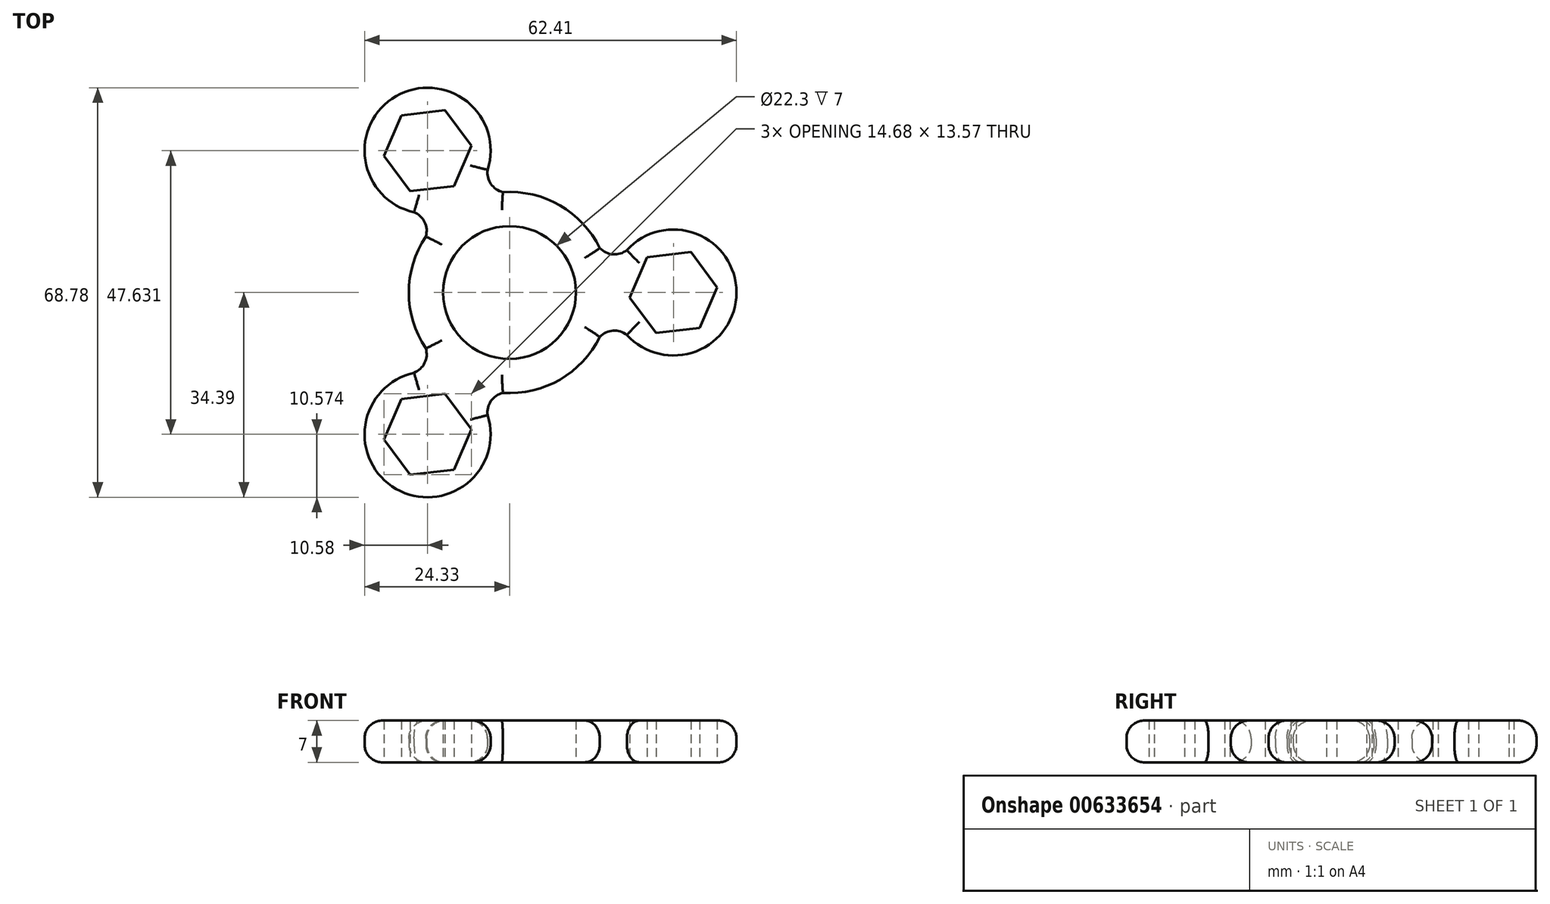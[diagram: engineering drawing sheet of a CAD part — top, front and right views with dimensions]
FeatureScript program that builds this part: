
annotation { "Feature Type Name" : "Feature", "Feature Type Description" : "" }
export const myFeature = defineFeature(function(context is Context, id is Id, definition is map)
    precondition{}
    {
        {
            var Q0;
            Q0=qCreatedBy(makeId("Top.planeOp"),FACE);
            var sketch = newSketch(context, id + "F0", { "sketchPlane" : qUnion([Q0])});
            skCircle(sketch, "E0", {"center": v(0, 0) * mm, "radius": 11.15 * mm});
            skCircle(sketch, "E1.cCircle", {"center": v(27.5, 0) * mm, "radius": 6.4 * mm, "construction": true});
            skLineSegment(sketch, "E1.0", {"start": v(34.84, 0.86) * mm, "end": v(31.91, -5.93) * mm});
            skLineSegment(sketch, "E1.1", {"start": v(31.91, -5.93) * mm, "end": v(24.57, -6.79) * mm});
            skLineSegment(sketch, "E1.2", {"start": v(24.57, -6.79) * mm, "end": v(20.16, -0.86) * mm});
            skLineSegment(sketch, "E1.3", {"start": v(20.16, -0.86) * mm, "end": v(23.09, 5.93) * mm});
            skLineSegment(sketch, "E1.4", {"start": v(23.09, 5.93) * mm, "end": v(30.43, 6.79) * mm});
            skLineSegment(sketch, "E1.5", {"start": v(30.43, 6.79) * mm, "end": v(34.84, 0.86) * mm});
            skPoint(sketch, "E1.0.midPoint", {"position": v(33.38, -2.54) * mm});
            skCircle(sketch, "E2", {"center": v(0, 0) * mm, "radius": 16.9 * mm});
            skCircle(sketch, "E3", {"center": v(27.5, 0) * mm, "radius": 10.58 * mm});
            skArc(sketch, "E4", {"start": v(19.69, -7.13) * mm, "mid": v(17.36, -6.42) * mm, "end": v(15.15, -7.46) * mm});
            skArc(sketch, "E5.MirrorCS", {"start": v(19.69, 7.13) * mm, "mid": v(17.36, 6.42) * mm, "end": v(15.15, 7.46) * mm});
            skLineSegment(sketch, "E6.1.0", {"start": v(-16.68, 17.03) * mm, "end": v(-21.1, 22.96) * mm});
            skCircle(sketch, "E6.1.1", {"center": v(-13.75, 23.82) * mm, "radius": 10.58 * mm});
            skLineSegment(sketch, "E6.1.2", {"start": v(-6.4, 24.67) * mm, "end": v(-9.34, 17.89) * mm});
            skCircle(sketch, "E6.1.3", {"center": v(-13.75, 23.82) * mm, "radius": 6.4 * mm, "construction": true});
            skPoint(sketch, "E6.1.4", {"position": v(-14.5, 30.17) * mm});
            skLineSegment(sketch, "E6.1.5", {"start": v(-10.82, 30.6) * mm, "end": v(-6.4, 24.67) * mm});
            skLineSegment(sketch, "E6.1.6", {"start": v(-9.34, 17.89) * mm, "end": v(-16.68, 17.03) * mm});
            skArc(sketch, "E6.1.7", {"start": v(-16.02, 13.49) * mm, "mid": v(-14.24, 11.82) * mm, "end": v(-14.04, 9.4) * mm});
            skArc(sketch, "E6.1.8", {"start": v(-3.67, 20.61) * mm, "mid": v(-3.12, 18.24) * mm, "end": v(-1.12, 16.86) * mm});
            skLineSegment(sketch, "E6.1.9", {"start": v(-18.16, 29.74) * mm, "end": v(-10.82, 30.6) * mm});
            skLineSegment(sketch, "E6.1.10", {"start": v(-21.1, 22.96) * mm, "end": v(-18.16, 29.74) * mm});
            skLineSegment(sketch, "E6.2.0", {"start": v(-6.4, -22.96) * mm, "end": v(-9.34, -29.74) * mm});
            skCircle(sketch, "E6.2.1", {"center": v(-13.75, -23.82) * mm, "radius": 10.58 * mm});
            skLineSegment(sketch, "E6.2.2", {"start": v(-18.16, -17.89) * mm, "end": v(-10.82, -17.03) * mm});
            skCircle(sketch, "E6.2.3", {"center": v(-13.75, -23.82) * mm, "radius": 6.4 * mm, "construction": true});
            skPoint(sketch, "E6.2.4", {"position": v(-18.88, -27.64) * mm});
            skLineSegment(sketch, "E6.2.5", {"start": v(-21.1, -24.67) * mm, "end": v(-18.16, -17.89) * mm});
            skLineSegment(sketch, "E6.2.6", {"start": v(-10.82, -17.03) * mm, "end": v(-6.4, -22.96) * mm});
            skArc(sketch, "E6.2.7", {"start": v(-3.67, -20.61) * mm, "mid": v(-3.12, -18.24) * mm, "end": v(-1.12, -16.86) * mm});
            skArc(sketch, "E6.2.8", {"start": v(-16.02, -13.49) * mm, "mid": v(-14.24, -11.82) * mm, "end": v(-14.04, -9.4) * mm});
            skLineSegment(sketch, "E6.2.9", {"start": v(-16.68, -30.6) * mm, "end": v(-21.1, -24.67) * mm});
            skLineSegment(sketch, "E6.2.10", {"start": v(-9.34, -29.74) * mm, "end": v(-16.68, -30.6) * mm});
            skSolve(sketch);
        }
        {
            var Q0;
            Q0 = qSketchRegion(id + "F0", true);
            extrude(context, id + "F1", {"entities" : qUnion([Q0]), "depth" : 7 * mm, "offsetDistance" : 25 * mm});
        }
        {
            var Q0;
            Q0=makeQuery(id+"F1.opExtrude","CAP_EDGE",EDGE,{"disambiguationData":[OSD([sQuery(id+"F0.wireOp",EDGE,"E6.1.1")])],"isStart":false});
            var Q1;
            Q1=makeQuery(id+"F1.opExtrude","CAP_EDGE",EDGE,{"disambiguationData":[OSD([sQuery(id+"F0.wireOp",EDGE,"E6.1.7")])],"isStart":false});
            var Q2;
            Q2=makeQuery(id+"F1.opExtrude","CAP_EDGE",EDGE,{"disambiguationData":[OSD([sQuery(id+"F0.wireOp",EDGE,"E6.1.1")])],"isStart":true});
            var Q3;
            {var subQ0=sQuery(id+"F0.wireOp",EDGE,"E2");Q3=makeQuery(id+"F1.opExtrude","CAP_EDGE",EDGE,{"disambiguationData":[OSD([subQ0]),TDD([makeQuery(id+"F0.imprint","IMPRINT",EDGE,{"disambiguationData":[TD([[makeQuery(id+"F0.imprint","INTERSECT",VERTEX,{"derivedFrom":[subQ0,sQuery(id+"F0.wireOp",EDGE,"E6.1.7")]}),-1.0]])],"derivedFrom":subQ0})])],"isStart":false});}
            var Q4;
            {var subQ0=sQuery(id+"F0.wireOp",EDGE,"E2");Q4=makeQuery(id+"F1.opExtrude","CAP_EDGE",EDGE,{"disambiguationData":[OSD([subQ0]),TDD([makeQuery(id+"F0.imprint","IMPRINT",EDGE,{"disambiguationData":[TD([[makeQuery(id+"F0.imprint","INTERSECT",VERTEX,{"derivedFrom":[subQ0,sQuery(id+"F0.wireOp",EDGE,"E6.1.7")]}),-1.0]])],"derivedFrom":subQ0})])],"isStart":true});}
            var Q5;
            Q5=makeQuery(id+"F1.opExtrude","CAP_EDGE",EDGE,{"disambiguationData":[OSD([sQuery(id+"F0.wireOp",EDGE,"E6.2.8")])],"isStart":false});
            var Q6;
            Q6=makeQuery(id+"F1.opExtrude","CAP_EDGE",EDGE,{"disambiguationData":[OSD([sQuery(id+"F0.wireOp",EDGE,"E6.2.1")])],"isStart":false});
            var Q7;
            Q7=makeQuery(id+"F1.opExtrude","CAP_EDGE",EDGE,{"disambiguationData":[OSD([sQuery(id+"F0.wireOp",EDGE,"E6.2.1")])],"isStart":true});
            var Q8;
            Q8=makeQuery(id+"F1.opExtrude","CAP_EDGE",EDGE,{"disambiguationData":[OSD([sQuery(id+"F0.wireOp",EDGE,"E6.2.7")])],"isStart":true});
            var Q9;
            {var subQ0=sQuery(id+"F0.wireOp",EDGE,"E2");Q9=makeQuery(id+"F1.opExtrude","CAP_EDGE",EDGE,{"disambiguationData":[OSD([subQ0]),TDD([makeQuery(id+"F0.imprint","IMPRINT",EDGE,{"disambiguationData":[TD([[makeQuery(id+"F0.imprint","INTERSECT",VERTEX,{"derivedFrom":[subQ0,sQuery(id+"F0.wireOp",EDGE,"E4")]}),1.0]])],"derivedFrom":subQ0})])],"isStart":false});}
            var Q10;
            Q10=makeQuery(id+"F1.opExtrude","CAP_EDGE",EDGE,{"disambiguationData":[OSD([sQuery(id+"F0.wireOp",EDGE,"E6.2.7")])],"isStart":false});
            var Q11;
            {var subQ0=sQuery(id+"F0.wireOp",EDGE,"E2");Q11=makeQuery(id+"F1.opExtrude","CAP_EDGE",EDGE,{"disambiguationData":[OSD([subQ0]),TDD([makeQuery(id+"F0.imprint","IMPRINT",EDGE,{"disambiguationData":[TD([[makeQuery(id+"F0.imprint","INTERSECT",VERTEX,{"derivedFrom":[subQ0,sQuery(id+"F0.wireOp",EDGE,"E4")]}),1.0]])],"derivedFrom":subQ0})])],"isStart":true});}
            var Q12;
            Q12=makeQuery(id+"F1.opExtrude","CAP_EDGE",EDGE,{"disambiguationData":[OSD([sQuery(id+"F0.wireOp",EDGE,"E4")])],"isStart":true});
            var Q13;
            Q13=makeQuery(id+"F1.opExtrude","CAP_EDGE",EDGE,{"disambiguationData":[OSD([sQuery(id+"F0.wireOp",EDGE,"E3")])],"isStart":false});
            var Q14;
            Q14=makeQuery(id+"F1.opExtrude","CAP_EDGE",EDGE,{"disambiguationData":[OSD([sQuery(id+"F0.wireOp",EDGE,"E4")])],"isStart":false});
            var Q15;
            Q15=makeQuery(id+"F1.opExtrude","CAP_EDGE",EDGE,{"disambiguationData":[OSD([sQuery(id+"F0.wireOp",EDGE,"E3")])],"isStart":true});
            var Q16;
            Q16=makeQuery(id+"F1.opExtrude","CAP_EDGE",EDGE,{"disambiguationData":[OSD([sQuery(id+"F0.wireOp",EDGE,"E5.MirrorCS")])],"isStart":false});
            var Q17;
            {var subQ0=sQuery(id+"F0.wireOp",EDGE,"E2");Q17=makeQuery(id+"F1.opExtrude","CAP_EDGE",EDGE,{"disambiguationData":[OSD([subQ0]),TDD([makeQuery(id+"F0.imprint","IMPRINT",EDGE,{"disambiguationData":[TD([[makeQuery(id+"F0.imprint","INTERSECT",VERTEX,{"derivedFrom":[subQ0,sQuery(id+"F0.wireOp",EDGE,"E5.MirrorCS")]}),-1.0]])],"derivedFrom":subQ0})])],"isStart":false});}
            var Q18;
            Q18=makeQuery(id+"F1.opExtrude","CAP_EDGE",EDGE,{"disambiguationData":[OSD([sQuery(id+"F0.wireOp",EDGE,"E6.1.8")])],"isStart":false});
            var Q19;
            Q19=makeQuery(id+"F1.opExtrude","CAP_EDGE",EDGE,{"disambiguationData":[OSD([sQuery(id+"F0.wireOp",EDGE,"E6.1.7")])],"isStart":true});
            var Q20;
            Q20=makeQuery(id+"F1.opExtrude","CAP_EDGE",EDGE,{"disambiguationData":[OSD([sQuery(id+"F0.wireOp",EDGE,"E6.2.8")])],"isStart":true});
            var Q21;
            {var subQ0=sQuery(id+"F0.wireOp",EDGE,"E2");Q21=makeQuery(id+"F1.opExtrude","CAP_EDGE",EDGE,{"disambiguationData":[OSD([subQ0]),TDD([makeQuery(id+"F0.imprint","IMPRINT",EDGE,{"disambiguationData":[TD([[makeQuery(id+"F0.imprint","INTERSECT",VERTEX,{"derivedFrom":[subQ0,sQuery(id+"F0.wireOp",EDGE,"E5.MirrorCS")]}),-1.0]])],"derivedFrom":subQ0})])],"isStart":true});}
            var Q22;
            Q22=makeQuery(id+"F1.opExtrude","CAP_EDGE",EDGE,{"disambiguationData":[OSD([sQuery(id+"F0.wireOp",EDGE,"E6.1.8")])],"isStart":true});
            var Q23;
            Q23=makeQuery(id+"F1.opExtrude","CAP_EDGE",EDGE,{"disambiguationData":[OSD([sQuery(id+"F0.wireOp",EDGE,"E5.MirrorCS")])],"isStart":true});
            fillet(context, id + "F2", {"entities" : qUnion([Q0, Q1, Q2, Q3, Q4, Q5, Q6, Q7, Q8, Q9, Q10, Q11, Q12, Q13, Q14, Q15, Q16, Q17, Q18, Q19, Q20, Q21, Q22, Q23]), "radius" : 3 * mm, "tangentPropagation" : true, "allowEdgeOverflow" : false});
        }
    });
